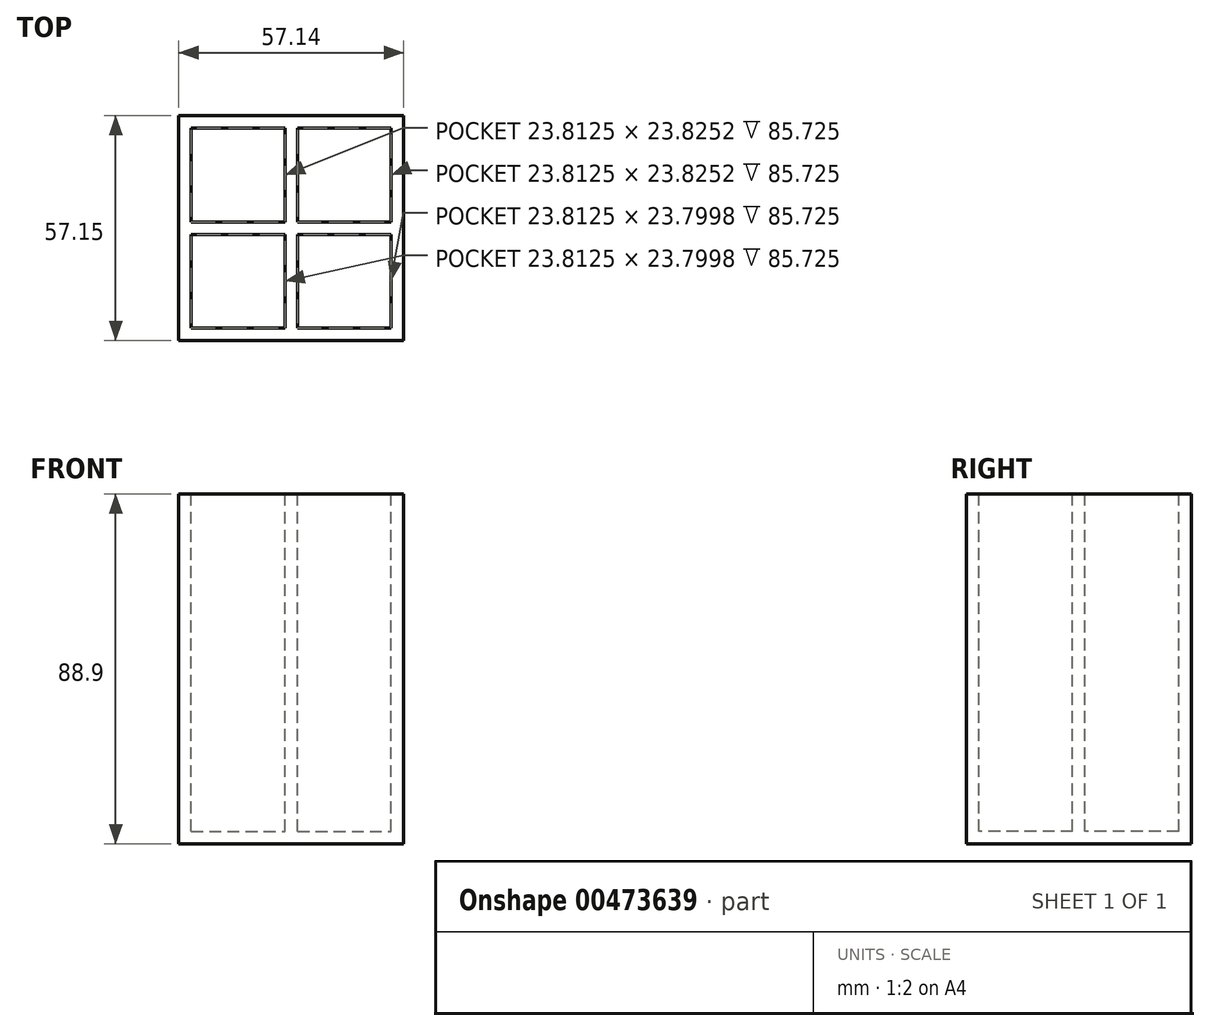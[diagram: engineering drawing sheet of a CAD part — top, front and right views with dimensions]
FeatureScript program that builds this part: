
annotation { "Feature Type Name" : "Feature", "Feature Type Description" : "" }
export const myFeature = defineFeature(function(context is Context, id is Id, definition is map)
    precondition{}
    {
        {
            var Q0;
            Q0=qCreatedBy(makeId("Front.planeOp"),FACE);
            var sketch = newSketch(context, id + "F0", { "sketchPlane" : qUnion([Q0])});
            skLineSegment(sketch, "E0.bottom", {"start": v(28.58, 44.45) * mm, "end": v(-28.58, 44.45) * mm});
            skLineSegment(sketch, "E0.top", {"start": v(28.58, -44.45) * mm, "end": v(-28.58, -44.45) * mm});
            skLineSegment(sketch, "E0.left", {"start": v(28.58, 44.45) * mm, "end": v(28.57, -44.45) * mm});
            skLineSegment(sketch, "E0.right", {"start": v(-28.58, 44.45) * mm, "end": v(-28.58, -44.45) * mm});
            skPoint(sketch, "E0.middle", {"position": v(0, 0) * mm});
            skSolve(sketch);
        }
        {
            var Q0;
            Q0 = qSketchRegion(id + "F0", true);
            extrude(context, id + "F1", {"entities" : qUnion([Q0]), "depth" : 57.15 * mm});
        }
        {
            var Q0;
            Q0=makeQuery(id+"F1.opExtrude","SWEPT_FACE",FACE,{"disambiguationData":[OSD([sQuery(id+"F0.wireOp",EDGE,"E0.bottom")])]});
            var sketch = newSketch(context, id + "F2", { "sketchPlane" : qUnion([Q0])});
            skLineSegment(sketch, "E1.bottom", {"start": v(-28.58, -3.18) * mm, "end": v(28.58, -3.18) * mm});
            skLineSegment(sketch, "E1.top", {"start": v(-28.58, 0) * mm, "end": v(28.58, 0) * mm});
            skLineSegment(sketch, "E1.left", {"start": v(-28.58, -3.18) * mm, "end": v(-28.58, 0) * mm});
            skLineSegment(sketch, "E1.right", {"start": v(28.58, -3.18) * mm, "end": v(28.58, 0) * mm});
            skLineSegment(sketch, "E2.bottom", {"start": v(-28.58, -53.98) * mm, "end": v(28.58, -53.98) * mm});
            skLineSegment(sketch, "E2.top", {"start": v(-28.58, -57.15) * mm, "end": v(28.58, -57.15) * mm});
            skLineSegment(sketch, "E2.left", {"start": v(-28.58, -53.98) * mm, "end": v(-28.58, -57.15) * mm});
            skLineSegment(sketch, "E2.right", {"start": v(28.58, -53.98) * mm, "end": v(28.58, -57.15) * mm});
            skLineSegment(sketch, "E3.bottom", {"start": v(-25.4, -3.18) * mm, "end": v(-28.58, -3.18) * mm});
            skLineSegment(sketch, "E3.top", {"start": v(-25.4, -53.98) * mm, "end": v(-28.58, -53.98) * mm});
            skLineSegment(sketch, "E3.left", {"start": v(-25.4, -3.18) * mm, "end": v(-25.4, -53.98) * mm});
            skLineSegment(sketch, "E3.right", {"start": v(-28.58, -3.18) * mm, "end": v(-28.58, -53.98) * mm});
            skLineSegment(sketch, "E4.bottom", {"start": v(25.4, -3.18) * mm, "end": v(28.58, -3.18) * mm});
            skLineSegment(sketch, "E4.top", {"start": v(25.4, -53.98) * mm, "end": v(28.58, -53.98) * mm});
            skLineSegment(sketch, "E4.left", {"start": v(25.4, -3.18) * mm, "end": v(25.4, -53.98) * mm});
            skLineSegment(sketch, "E4.right", {"start": v(28.58, -3.18) * mm, "end": v(28.58, -53.98) * mm});
            skLineSegment(sketch, "E5.bottom", {"start": v(-1.59, -3.18) * mm, "end": v(1.59, -3.18) * mm});
            skLineSegment(sketch, "E5.top", {"start": v(-1.59, -53.98) * mm, "end": v(1.59, -53.98) * mm});
            skLineSegment(sketch, "E5.left", {"start": v(-1.59, -3.18) * mm, "end": v(-1.59, -53.98) * mm});
            skLineSegment(sketch, "E5.right", {"start": v(1.59, -3.18) * mm, "end": v(1.59, -53.98) * mm});
            skLineSegment(sketch, "E6.bottom", {"start": v(-25.4, -30.18) * mm, "end": v(25.4, -30.18) * mm});
            skLineSegment(sketch, "E6.top", {"start": v(-25.4, -27) * mm, "end": v(25.4, -27) * mm});
            skLineSegment(sketch, "E6.left", {"start": v(-25.4, -30.18) * mm, "end": v(-25.4, -27) * mm});
            skLineSegment(sketch, "E6.right", {"start": v(25.4, -30.18) * mm, "end": v(25.4, -27) * mm});
            skSolve(sketch);
        }
        {
            var Q0;
            {var subQ3=sQuery(id+"F2.wireOp",EDGE,"E5.left");var subQ5=sQuery(id+"F2.wireOp",EDGE,"E6.top");var subQ7=makeQuery(id+"F2.imprint","INTERSECT",VERTEX,{"derivedFrom":[subQ3,subQ5]});Q0=makeQuery(id+"F2.imprint","IMPRINT",FACE,{"disambiguationData":[TD([[makeQuery(id+"F2.imprint","IMPRINT",EDGE,{"disambiguationData":[TD([[subQ7,1.0]])],"derivedFrom":subQ3}),-1.0]])]});}
            var Q1;
            {var subQ3=sQuery(id+"F2.wireOp",EDGE,"E5.right");var subQ5=sQuery(id+"F2.wireOp",EDGE,"E6.top");var subQ7=makeQuery(id+"F2.imprint","INTERSECT",VERTEX,{"derivedFrom":[subQ3,subQ5]});Q1=makeQuery(id+"F2.imprint","IMPRINT",FACE,{"disambiguationData":[TD([[makeQuery(id+"F2.imprint","IMPRINT",EDGE,{"disambiguationData":[TD([[subQ7,1.0]])],"derivedFrom":subQ3}),1.0]])]});}
            var Q2;
            {var subQ3=sQuery(id+"F2.wireOp",EDGE,"E5.right");var subQ5=sQuery(id+"F2.wireOp",EDGE,"E6.bottom");var subQ7=makeQuery(id+"F2.imprint","INTERSECT",VERTEX,{"derivedFrom":[subQ3,subQ5]});Q2=makeQuery(id+"F2.imprint","IMPRINT",FACE,{"disambiguationData":[TD([[makeQuery(id+"F2.imprint","IMPRINT",EDGE,{"disambiguationData":[TD([[subQ7,-1.0]])],"derivedFrom":subQ3}),1.0]])]});}
            var Q3;
            {var subQ3=sQuery(id+"F2.wireOp",EDGE,"E5.left");var subQ5=sQuery(id+"F2.wireOp",EDGE,"E6.bottom");var subQ7=makeQuery(id+"F2.imprint","INTERSECT",VERTEX,{"derivedFrom":[subQ3,subQ5]});Q3=makeQuery(id+"F2.imprint","IMPRINT",FACE,{"disambiguationData":[TD([[makeQuery(id+"F2.imprint","IMPRINT",EDGE,{"disambiguationData":[TD([[subQ7,-1.0]])],"derivedFrom":subQ3}),-1.0]])]});}
            extrude(context, id + "F3", {"entities" : qUnion([Q0, Q1, Q2, Q3]), "operationType" : NewBodyOperationType.REMOVE, "oppositeDirection" : true, "depth" : 85.72 * mm});
        }
    });
